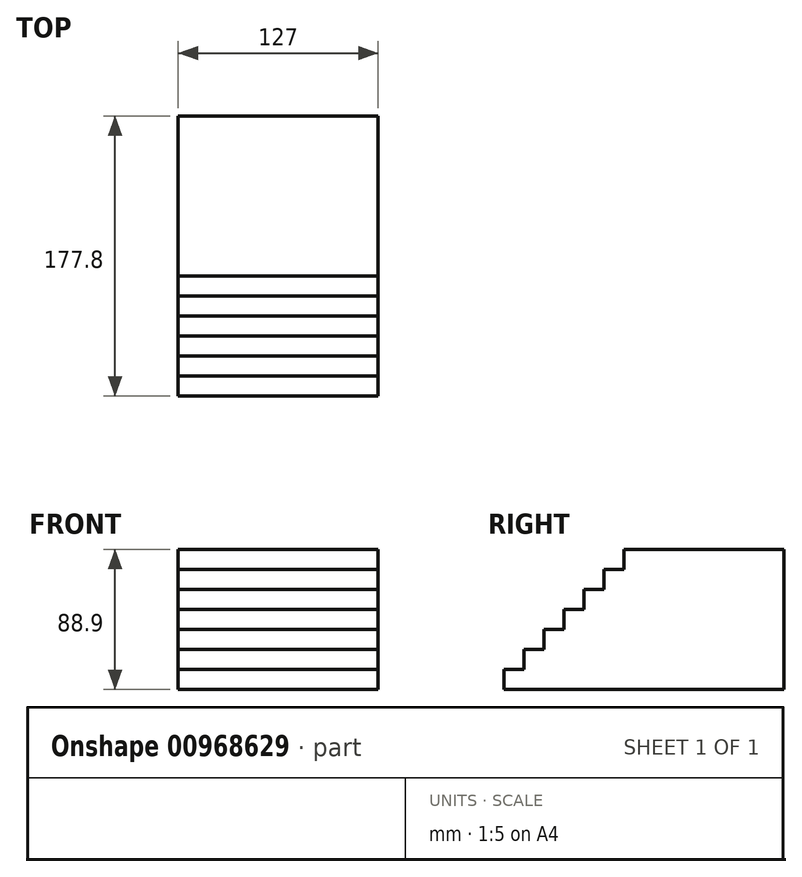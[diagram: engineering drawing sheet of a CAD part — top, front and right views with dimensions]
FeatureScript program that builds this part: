
annotation { "Feature Type Name" : "Feature", "Feature Type Description" : "" }
export const myFeature = defineFeature(function(context is Context, id is Id, definition is map)
    precondition{}
    {
        {
            var Q0;
            Q0=qCreatedBy(makeId("Top.planeOp"),FACE);
            var sketch = newSketch(context, id + "F0", { "sketchPlane" : qUnion([Q0])});
            skLineSegment(sketch, "E0.bottom", {"start": v(63.5, 88.9) * mm, "end": v(-63.5, 88.9) * mm});
            skLineSegment(sketch, "E0.top", {"start": v(63.5, -88.9) * mm, "end": v(-63.5, -88.9) * mm});
            skLineSegment(sketch, "E0.left", {"start": v(63.5, 88.9) * mm, "end": v(63.5, -88.9) * mm});
            skLineSegment(sketch, "E0.right", {"start": v(-63.5, 88.9) * mm, "end": v(-63.5, -88.9) * mm});
            skPoint(sketch, "E0.middle", {"position": v(0, 0) * mm});
            skSolve(sketch);
        }
        {
            var Q0;
            Q0=makeQuery(id+"F0.imprint","IMPRINT",FACE,{"disambiguationData":[TD([[makeQuery(id+"F0.imprint","IMPRINT",EDGE,{"derivedFrom":sQuery(id+"F0.wireOp",EDGE,"E0.bottom")}),1.0]])]});
            extrude(context, id + "F1", {"entities" : qUnion([Q0]), "depth" : 12.7 * mm, "offsetDistance" : 25.4 * mm});
        }
        {
            var Q0;
            Q0=makeQuery(id+"F1.opExtrude","CAP_FACE",FACE,{"disambiguationData":[OSD([sQuery(id+"F0.wireOp",EDGE,"E0.bottom"),sQuery(id+"F0.wireOp",EDGE,"E0.top"),sQuery(id+"F0.wireOp",EDGE,"E0.left"),sQuery(id+"F0.wireOp",EDGE,"E0.right")])],"isStart":false});
            var sketch = newSketch(context, id + "F2", { "sketchPlane" : qUnion([Q0])});
            skLineSegment(sketch, "E1.bottom", {"start": v(-63.5, 88.9) * mm, "end": v(63.5, 88.9) * mm});
            skLineSegment(sketch, "E1.top", {"start": v(-63.5, -76.2) * mm, "end": v(63.5, -76.2) * mm});
            skLineSegment(sketch, "E1.left", {"start": v(-63.5, 88.9) * mm, "end": v(-63.5, -76.2) * mm});
            skLineSegment(sketch, "E1.right", {"start": v(63.5, 88.9) * mm, "end": v(63.5, -76.2) * mm});
            skSolve(sketch);
        }
        {
            var Q0;
            Q0=makeQuery(id+"F2.imprint","IMPRINT",FACE,{"disambiguationData":[TD([[makeQuery(id+"F2.imprint","IMPRINT",EDGE,{"derivedFrom":sQuery(id+"F2.wireOp",EDGE,"E1.bottom")}),1.0]])]});
            extrude(context, id + "F3", {"entities" : qUnion([Q0]), "operationType" : NewBodyOperationType.ADD, "depth" : 12.7 * mm, "offsetDistance" : 25.4 * mm});
        }
        {
            var Q0;
            Q0=makeQuery(id+"F3.opExtrude","CAP_FACE",FACE,{"disambiguationData":[OSD([sQuery(id+"F2.wireOp",EDGE,"E1.bottom"),sQuery(id+"F2.wireOp",EDGE,"E1.top"),sQuery(id+"F2.wireOp",EDGE,"E1.left"),sQuery(id+"F2.wireOp",EDGE,"E1.right")])],"isStart":false});
            var sketch = newSketch(context, id + "F4", { "sketchPlane" : qUnion([Q0])});
            skLineSegment(sketch, "E2.bottom", {"start": v(-63.5, 88.9) * mm, "end": v(63.5, 88.9) * mm});
            skLineSegment(sketch, "E2.top", {"start": v(-63.5, -63.5) * mm, "end": v(63.5, -63.5) * mm});
            skLineSegment(sketch, "E2.left", {"start": v(-63.5, 88.9) * mm, "end": v(-63.5, -63.5) * mm});
            skLineSegment(sketch, "E2.right", {"start": v(63.5, 88.9) * mm, "end": v(63.5, -63.5) * mm});
            skSolve(sketch);
        }
        {
            var Q0;
            Q0=makeQuery(id+"F4.imprint","IMPRINT",FACE,{"disambiguationData":[TD([[makeQuery(id+"F4.imprint","IMPRINT",EDGE,{"derivedFrom":sQuery(id+"F4.wireOp",EDGE,"E2.bottom")}),1.0]])]});
            extrude(context, id + "F5", {"entities" : qUnion([Q0]), "operationType" : NewBodyOperationType.ADD, "depth" : 12.7 * mm, "offsetDistance" : 25.4 * mm});
        }
        {
            var Q0;
            Q0=makeQuery(id+"F5.opExtrude","CAP_FACE",FACE,{"disambiguationData":[OSD([sQuery(id+"F4.wireOp",EDGE,"E2.bottom"),sQuery(id+"F4.wireOp",EDGE,"E2.top"),sQuery(id+"F4.wireOp",EDGE,"E2.left"),sQuery(id+"F4.wireOp",EDGE,"E2.right")])],"isStart":false});
            var sketch = newSketch(context, id + "F6", { "sketchPlane" : qUnion([Q0])});
            skLineSegment(sketch, "E3.bottom", {"start": v(-63.5, 88.9) * mm, "end": v(63.5, 88.9) * mm});
            skLineSegment(sketch, "E3.top", {"start": v(-63.5, -50.8) * mm, "end": v(63.5, -50.8) * mm});
            skLineSegment(sketch, "E3.left", {"start": v(-63.5, 88.9) * mm, "end": v(-63.5, -50.8) * mm});
            skLineSegment(sketch, "E3.right", {"start": v(63.5, 88.9) * mm, "end": v(63.5, -50.8) * mm});
            skSolve(sketch);
        }
        {
            var Q0;
            Q0=makeQuery(id+"F6.imprint","IMPRINT",FACE,{"disambiguationData":[TD([[makeQuery(id+"F6.imprint","IMPRINT",EDGE,{"derivedFrom":sQuery(id+"F6.wireOp",EDGE,"E3.bottom")}),1.0]])]});
            extrude(context, id + "F7", {"entities" : qUnion([Q0]), "operationType" : NewBodyOperationType.ADD, "depth" : 12.7 * mm, "offsetDistance" : 25.4 * mm});
        }
        {
            var Q0;
            Q0=makeQuery(id+"F7.opExtrude","CAP_FACE",FACE,{"disambiguationData":[OSD([sQuery(id+"F6.wireOp",EDGE,"E3.bottom"),sQuery(id+"F6.wireOp",EDGE,"E3.top"),sQuery(id+"F6.wireOp",EDGE,"E3.left"),sQuery(id+"F6.wireOp",EDGE,"E3.right")])],"isStart":false});
            var sketch = newSketch(context, id + "F8", { "sketchPlane" : qUnion([Q0])});
            skLineSegment(sketch, "E4.bottom", {"start": v(-63.5, 88.9) * mm, "end": v(63.5, 88.9) * mm});
            skLineSegment(sketch, "E4.top", {"start": v(-63.5, -38.1) * mm, "end": v(63.5, -38.1) * mm});
            skLineSegment(sketch, "E4.left", {"start": v(-63.5, 88.9) * mm, "end": v(-63.5, -38.1) * mm});
            skLineSegment(sketch, "E4.right", {"start": v(63.5, 88.9) * mm, "end": v(63.5, -38.1) * mm});
            skSolve(sketch);
        }
        {
            var Q0;
            Q0=makeQuery(id+"F8.imprint","IMPRINT",FACE,{"disambiguationData":[TD([[makeQuery(id+"F8.imprint","IMPRINT",EDGE,{"derivedFrom":sQuery(id+"F8.wireOp",EDGE,"E4.bottom")}),1.0]])]});
            extrude(context, id + "F9", {"entities" : qUnion([Q0]), "operationType" : NewBodyOperationType.ADD, "depth" : 12.7 * mm, "offsetDistance" : 25.4 * mm});
        }
        {
            var Q0;
            Q0=makeQuery(id+"F9.opExtrude","CAP_FACE",FACE,{"disambiguationData":[OSD([sQuery(id+"F8.wireOp",EDGE,"E4.bottom"),sQuery(id+"F8.wireOp",EDGE,"E4.top"),sQuery(id+"F8.wireOp",EDGE,"E4.left"),sQuery(id+"F8.wireOp",EDGE,"E4.right")])],"isStart":false});
            var sketch = newSketch(context, id + "F10", { "sketchPlane" : qUnion([Q0])});
            skLineSegment(sketch, "E5.bottom", {"start": v(-63.5, 88.9) * mm, "end": v(63.5, 88.9) * mm});
            skLineSegment(sketch, "E5.top", {"start": v(-63.5, -25.4) * mm, "end": v(63.5, -25.4) * mm});
            skLineSegment(sketch, "E5.left", {"start": v(-63.5, 88.9) * mm, "end": v(-63.5, -25.4) * mm});
            skLineSegment(sketch, "E5.right", {"start": v(63.5, 88.9) * mm, "end": v(63.5, -25.4) * mm});
            skSolve(sketch);
        }
        {
            var Q0;
            Q0=makeQuery(id+"F10.imprint","IMPRINT",FACE,{"disambiguationData":[TD([[makeQuery(id+"F10.imprint","IMPRINT",EDGE,{"derivedFrom":sQuery(id+"F10.wireOp",EDGE,"E5.bottom")}),1.0]])]});
            extrude(context, id + "F11", {"entities" : qUnion([Q0]), "operationType" : NewBodyOperationType.ADD, "depth" : 12.7 * mm, "offsetDistance" : 25.4 * mm});
        }
        {
            var Q0;
            Q0=makeQuery(id+"F11.opExtrude","CAP_FACE",FACE,{"disambiguationData":[OSD([sQuery(id+"F10.wireOp",EDGE,"E5.bottom"),sQuery(id+"F10.wireOp",EDGE,"E5.top"),sQuery(id+"F10.wireOp",EDGE,"E5.left"),sQuery(id+"F10.wireOp",EDGE,"E5.right")])],"isStart":false});
            var sketch = newSketch(context, id + "F12", { "sketchPlane" : qUnion([Q0])});
            skLineSegment(sketch, "E6.bottom", {"start": v(-63.5, 88.9) * mm, "end": v(63.5, 88.9) * mm});
            skLineSegment(sketch, "E6.top", {"start": v(-63.5, -12.7) * mm, "end": v(63.5, -12.7) * mm});
            skLineSegment(sketch, "E6.left", {"start": v(-63.5, 88.9) * mm, "end": v(-63.5, -12.7) * mm});
            skLineSegment(sketch, "E6.right", {"start": v(63.5, 88.9) * mm, "end": v(63.5, -12.7) * mm});
            skSolve(sketch);
        }
        {
            var Q0;
            Q0=makeQuery(id+"F12.imprint","IMPRINT",FACE,{"disambiguationData":[TD([[makeQuery(id+"F12.imprint","IMPRINT",EDGE,{"derivedFrom":sQuery(id+"F12.wireOp",EDGE,"E6.bottom")}),1.0]])]});
            extrude(context, id + "F13", {"entities" : qUnion([Q0]), "operationType" : NewBodyOperationType.ADD, "depth" : 12.7 * mm, "offsetDistance" : 25.4 * mm});
        }
    });
